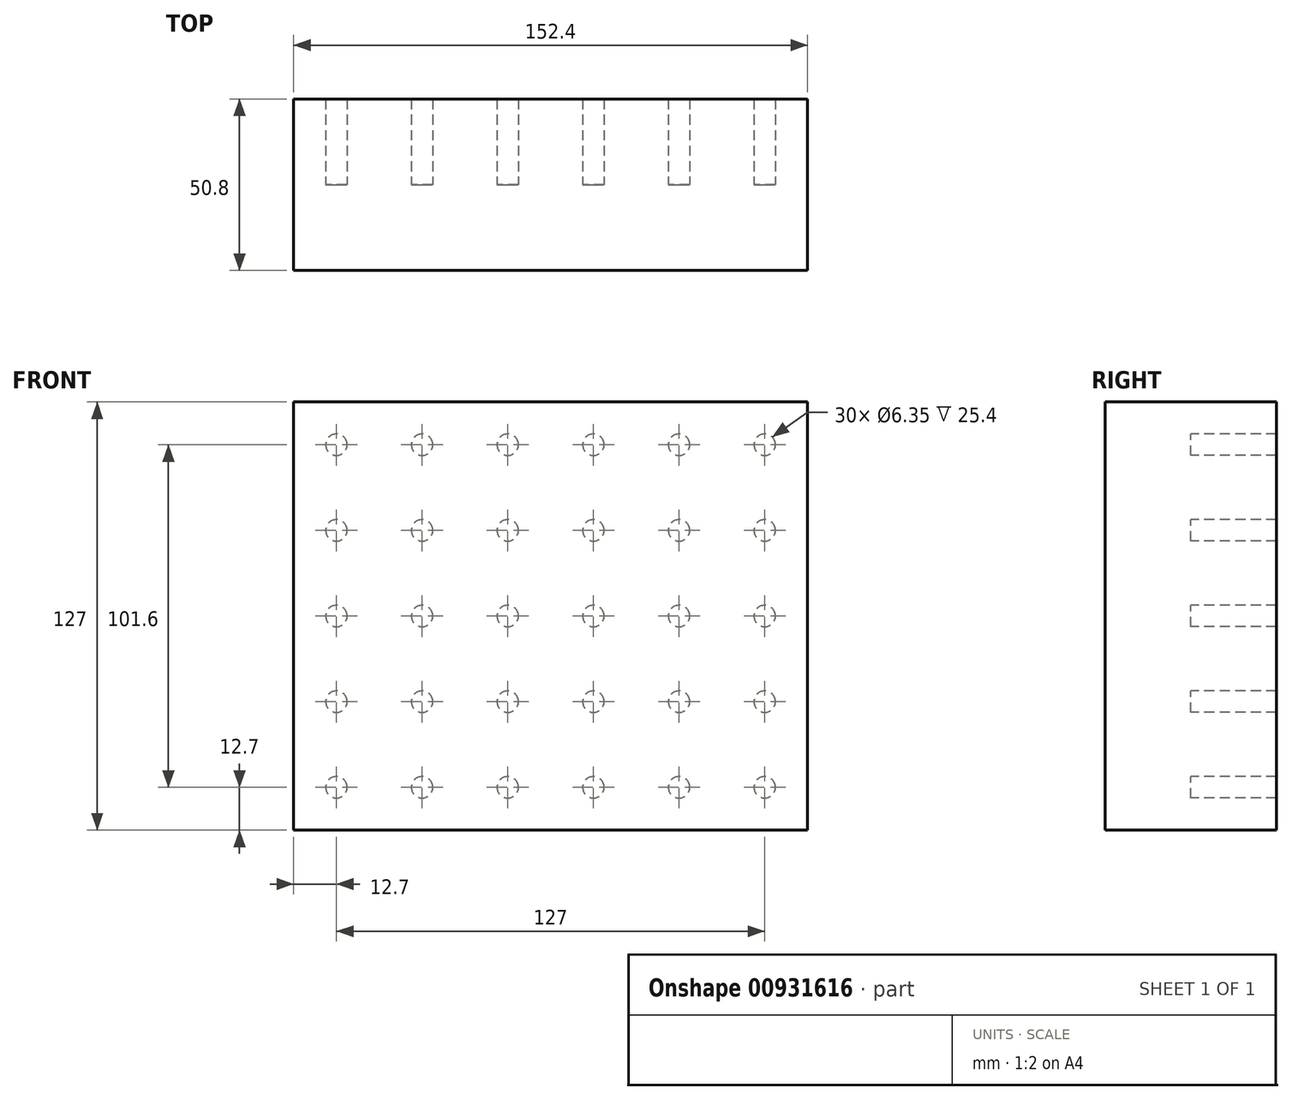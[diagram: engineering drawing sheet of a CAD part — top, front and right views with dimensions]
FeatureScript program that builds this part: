
annotation { "Feature Type Name" : "Feature", "Feature Type Description" : "" }
export const myFeature = defineFeature(function(context is Context, id is Id, definition is map)
    precondition{}
    {
        {
            var Q0;
            Q0=qCreatedBy(makeId("Front.planeOp"),FACE);
            var sketch = newSketch(context, id + "F0", { "sketchPlane" : qUnion([Q0])});
            skLineSegment(sketch, "E0.bottom", {"start": v(76.2, 63.5) * mm, "end": v(-76.2, 63.5) * mm});
            skLineSegment(sketch, "E0.top", {"start": v(76.2, -63.5) * mm, "end": v(-76.2, -63.5) * mm});
            skLineSegment(sketch, "E0.left", {"start": v(76.2, 63.5) * mm, "end": v(76.2, -63.5) * mm});
            skLineSegment(sketch, "E0.right", {"start": v(-76.2, 63.5) * mm, "end": v(-76.2, -63.5) * mm});
            skPoint(sketch, "E0.middle", {"position": v(0, 0) * mm});
            skSolve(sketch);
        }
        {
            var Q0;
            Q0=makeQuery(id+"F0.imprint","IMPRINT",FACE,{"disambiguationData":[TD([[makeQuery(id+"F0.imprint","IMPRINT",EDGE,{"derivedFrom":sQuery(id+"F0.wireOp",EDGE,"E0.bottom")}),1.0]])]});
            extrude(context, id + "F1", {"entities" : qUnion([Q0]), "endBound" : BoundingType.SYMMETRIC, "depth" : 50.8 * mm, "offsetDistance" : 25.4 * mm});
        }
        {
            var Q0;
            Q0=qCreatedBy(makeId("Front.planeOp"),FACE);
            var sketch = newSketch(context, id + "F2", { "sketchPlane" : qUnion([Q0])});
            skCircle(sketch, "E1", {"center": v(-63.5, 50.8) * mm, "radius": 6.35 * mm});
            skCircle(sketch, "E2", {"center": v(-38.1, 50.8) * mm, "radius": 6.35 * mm});
            skCircle(sketch, "E3", {"center": v(-12.7, 25.4) * mm, "radius": 6.35 * mm});
            skCircle(sketch, "E4", {"center": v(-38.1, 25.4) * mm, "radius": 6.35 * mm});
            skCircle(sketch, "E5", {"center": v(-63.5, 25.4) * mm, "radius": 6.35 * mm});
            skCircle(sketch, "E6", {"center": v(-12.7, 0) * mm, "radius": 6.35 * mm});
            skCircle(sketch, "E7", {"center": v(-63.5, 0) * mm, "radius": 6.35 * mm});
            skCircle(sketch, "E8", {"center": v(-38.1, 0) * mm, "radius": 6.35 * mm});
            skCircle(sketch, "E9", {"center": v(-12.7, 50.8) * mm, "radius": 6.35 * mm});
            skCircle(sketch, "E10.MirrorC", {"center": v(12.7, 25.4) * mm, "radius": 6.35 * mm});
            skCircle(sketch, "E11.MirrorC", {"center": v(63.5, 25.4) * mm, "radius": 6.35 * mm});
            skCircle(sketch, "E12.MirrorC", {"center": v(12.7, 0) * mm, "radius": 6.35 * mm});
            skCircle(sketch, "E13.MirrorC", {"center": v(63.5, 0) * mm, "radius": 6.35 * mm});
            skCircle(sketch, "E14.MirrorC", {"center": v(63.5, 50.8) * mm, "radius": 6.35 * mm});
            skCircle(sketch, "E15.MirrorC", {"center": v(38.1, 0) * mm, "radius": 6.35 * mm});
            skCircle(sketch, "E16.MirrorC", {"center": v(38.1, 50.8) * mm, "radius": 6.35 * mm});
            skCircle(sketch, "E17.MirrorC", {"center": v(38.1, 25.4) * mm, "radius": 6.35 * mm});
            skCircle(sketch, "E18.MirrorC", {"center": v(12.7, 50.8) * mm, "radius": 6.35 * mm});
            skCircle(sketch, "E19.MirrorC", {"center": v(-63.5, -50.8) * mm, "radius": 6.35 * mm});
            skCircle(sketch, "E20.MirrorC", {"center": v(-12.7, -25.4) * mm, "radius": 6.35 * mm});
            skCircle(sketch, "E21.MirrorC", {"center": v(-38.1, -50.8) * mm, "radius": 6.35 * mm});
            skCircle(sketch, "E22.MirrorC", {"center": v(12.7, -25.4) * mm, "radius": 6.35 * mm});
            skCircle(sketch, "E23.MirrorC", {"center": v(-38.1, -25.4) * mm, "radius": 6.35 * mm});
            skCircle(sketch, "E24.MirrorC", {"center": v(-63.5, -25.4) * mm, "radius": 6.35 * mm});
            skCircle(sketch, "E25.MirrorC", {"center": v(-12.7, -50.8) * mm, "radius": 6.35 * mm});
            skCircle(sketch, "E26.MirrorC", {"center": v(38.1, -50.8) * mm, "radius": 6.35 * mm});
            skCircle(sketch, "E27.MirrorC", {"center": v(63.5, -25.4) * mm, "radius": 6.35 * mm});
            skCircle(sketch, "E28.MirrorC", {"center": v(12.7, -50.8) * mm, "radius": 6.35 * mm});
            skCircle(sketch, "E29.MirrorC", {"center": v(63.5, -50.8) * mm, "radius": 6.35 * mm});
            skCircle(sketch, "E30.MirrorC", {"center": v(38.1, -25.4) * mm, "radius": 6.35 * mm});
            skSolve(sketch);
        }
        {
            var Q0;
            Q0=sQuery(id+"F2.wireOp",VERTEX,"E1.center");
            var Q1;
            Q1=sQuery(id+"F2.wireOp",VERTEX,"E2.center");
            var Q2;
            Q2=sQuery(id+"F2.wireOp",VERTEX,"E5.center");
            var Q3;
            Q3=sQuery(id+"F2.wireOp",VERTEX,"E4.center");
            var Q4;
            Q4=sQuery(id+"F2.wireOp",VERTEX,"E9.center");
            var Q5;
            Q5=sQuery(id+"F2.wireOp",VERTEX,"E3.center");
            var Q6;
            Q6=sQuery(id+"F2.wireOp",VERTEX,"E18.MirrorC.center");
            var Q7;
            Q7=sQuery(id+"F2.wireOp",VERTEX,"E16.MirrorC.center");
            var Q8;
            Q8=sQuery(id+"F2.wireOp",VERTEX,"E14.MirrorC.center");
            var Q9;
            Q9=sQuery(id+"F2.wireOp",VERTEX,"E11.MirrorC.center");
            var Q10;
            Q10=sQuery(id+"F2.wireOp",VERTEX,"E17.MirrorC.center");
            var Q11;
            Q11=sQuery(id+"F2.wireOp",VERTEX,"E10.MirrorC.center");
            var Q12;
            Q12=sQuery(id+"F2.wireOp",VERTEX,"E7.center");
            var Q13;
            Q13=sQuery(id+"F2.wireOp",VERTEX,"E8.center");
            var Q14;
            Q14=sQuery(id+"F2.wireOp",VERTEX,"E6.center");
            var Q15;
            Q15=sQuery(id+"F2.wireOp",VERTEX,"E12.MirrorC.center");
            var Q16;
            Q16=sQuery(id+"F2.wireOp",VERTEX,"E15.MirrorC.center");
            var Q17;
            Q17=sQuery(id+"F2.wireOp",VERTEX,"E13.MirrorC.center");
            var Q18;
            Q18=sQuery(id+"F2.wireOp",VERTEX,"E27.MirrorC.center");
            var Q19;
            Q19=sQuery(id+"F2.wireOp",VERTEX,"E29.MirrorC.center");
            var Q20;
            Q20=sQuery(id+"F2.wireOp",VERTEX,"E26.MirrorC.center");
            var Q21;
            Q21=sQuery(id+"F2.wireOp",VERTEX,"E30.MirrorC.center");
            var Q22;
            Q22=sQuery(id+"F2.wireOp",VERTEX,"E22.MirrorC.center");
            var Q23;
            Q23=sQuery(id+"F2.wireOp",VERTEX,"E28.MirrorC.center");
            var Q24;
            Q24=sQuery(id+"F2.wireOp",VERTEX,"E25.MirrorC.center");
            var Q25;
            Q25=sQuery(id+"F2.wireOp",VERTEX,"E20.MirrorC.center");
            var Q26;
            Q26=sQuery(id+"F2.wireOp",VERTEX,"E23.MirrorC.center");
            var Q27;
            Q27=sQuery(id+"F2.wireOp",VERTEX,"E21.MirrorC.center");
            var Q28;
            Q28=sQuery(id+"F2.wireOp",VERTEX,"E19.MirrorC.center");
            var Q29;
            Q29=sQuery(id+"F2.wireOp",VERTEX,"E24.MirrorC.center");
            var Q30;
            Q30=makeQuery(id+"F1.opExtrude","SWEPT_BODY",BODY,{"disambiguationData":[OSD([sQuery(id+"F0.wireOp",EDGE,"E0.bottom"),sQuery(id+"F0.wireOp",EDGE,"E0.top"),sQuery(id+"F0.wireOp",EDGE,"E0.left"),sQuery(id+"F0.wireOp",EDGE,"E0.right")])]});
            hole(context, id + "F3", {"style" : HoleStyle.SIMPLE, "endStyle" : HoleEndStyle.THROUGH, "holeDiameter" : 6.35 * mm, "majorDiameter" : 6.35 * mm, "isTappedThrough" : true, "tappedDepth" : 12.7 * mm, "tapClearance" : 3, "locations" : qUnion([Q0, Q1, Q2, Q3, Q4, Q5, Q6, Q7, Q8, Q9, Q10, Q11, Q12, Q13, Q14, Q15, Q16, Q17, Q18, Q19, Q20, Q21, Q22, Q23, Q24, Q25, Q26, Q27, Q28, Q29]), "scope" : qUnion([Q30])});
        }
    });
